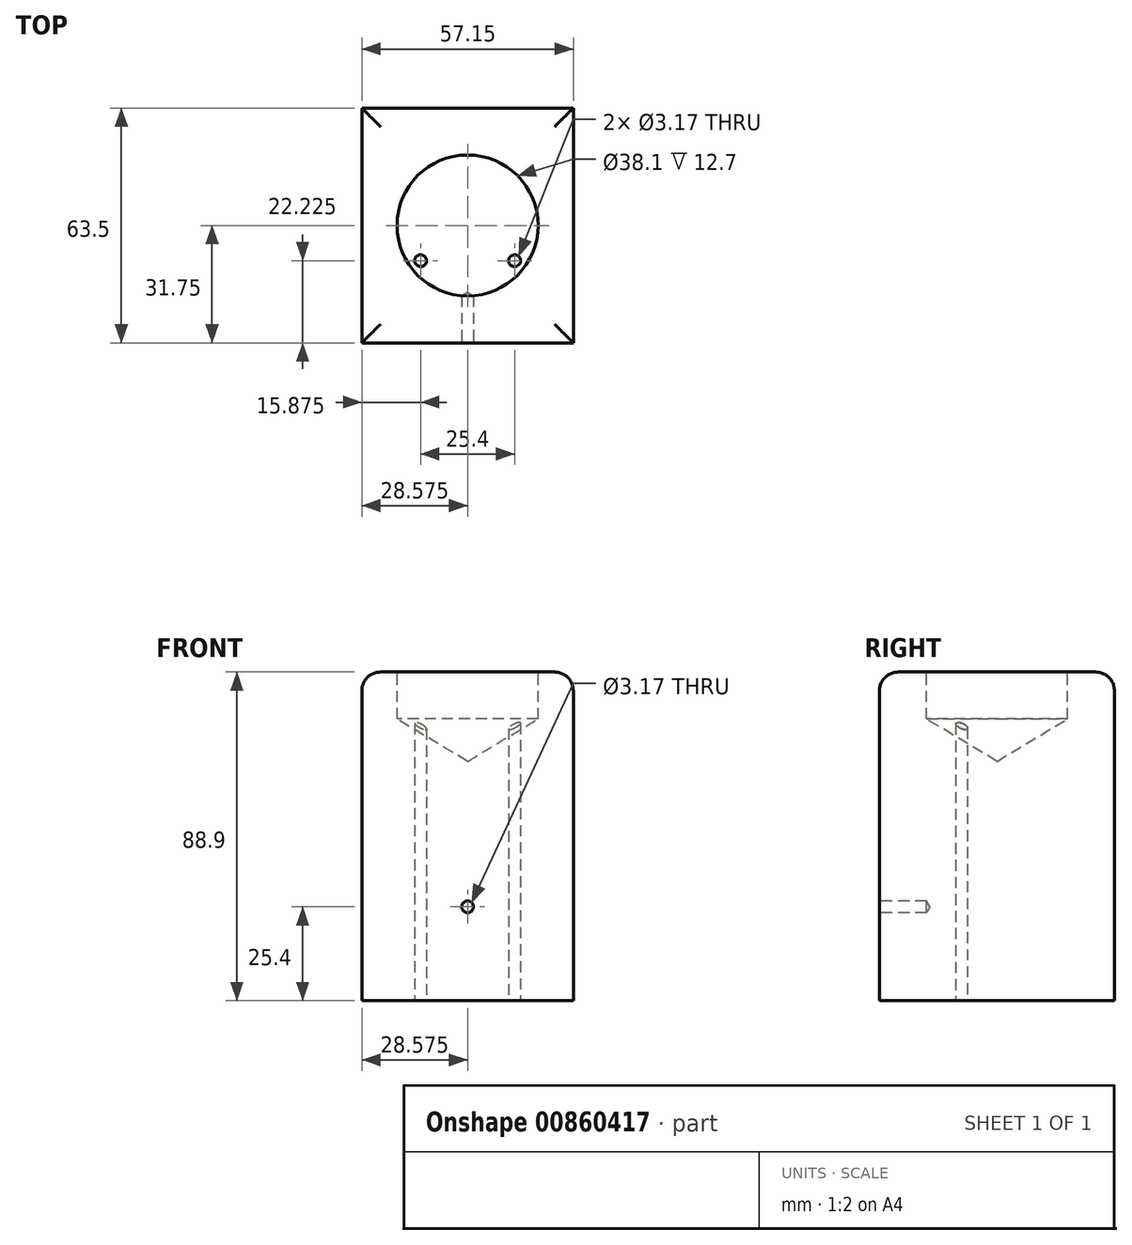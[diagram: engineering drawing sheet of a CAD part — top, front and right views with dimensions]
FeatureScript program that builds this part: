
annotation { "Feature Type Name" : "Feature", "Feature Type Description" : "" }
export const myFeature = defineFeature(function(context is Context, id is Id, definition is map)
    precondition{}
    {
        {
            var Q0;
            Q0=qCreatedBy(makeId("Top.planeOp"),FACE);
            var sketch = newSketch(context, id + "F0", { "sketchPlane" : qUnion([Q0])});
            skLineSegment(sketch, "E0.bottom", {"start": v(0, 0) * mm, "end": v(57.15, 0) * mm});
            skLineSegment(sketch, "E0.top", {"start": v(0, -63.5) * mm, "end": v(57.15, -63.5) * mm});
            skLineSegment(sketch, "E0.left", {"start": v(0, 0) * mm, "end": v(0, -63.5) * mm});
            skLineSegment(sketch, "E0.right", {"start": v(57.15, 0) * mm, "end": v(57.15, -63.5) * mm});
            skSolve(sketch);
        }
        {
            var Q0;
            Q0=makeQuery(id+"F0.imprint","IMPRINT",FACE,{"disambiguationData":[TD([[makeQuery(id+"F0.imprint","IMPRINT",EDGE,{"derivedFrom":sQuery(id+"F0.wireOp",EDGE,"E0.bottom")}),-1.0]])]});
            extrude(context, id + "F1", {"entities" : qUnion([Q0]), "depth" : 88.9 * mm, "offsetDistance" : 25.4 * mm});
        }
        {
            var Q0;
            Q0=makeQuery(id+"F1.opExtrude","CAP_FACE",FACE,{"disambiguationData":[OSD([sQuery(id+"F0.wireOp",EDGE,"E0.bottom"),sQuery(id+"F0.wireOp",EDGE,"E0.top"),sQuery(id+"F0.wireOp",EDGE,"E0.left"),sQuery(id+"F0.wireOp",EDGE,"E0.right")])],"isStart":false});
            var sketch = newSketch(context, id + "F2", { "sketchPlane" : qUnion([Q0])});
            skLineSegment(sketch, "E1", {"start": v(28.58, 0) * mm, "end": v(28.58, -63.5) * mm, "construction": true});
            skLineSegment(sketch, "E2", {"start": v(0, -31.75) * mm, "end": v(57.15, -31.75) * mm, "construction": true});
            skPoint(sketch, "E3", {"position": v(28.58, -31.75) * mm});
            skSolve(sketch);
        }
        {
            var Q0;
            Q0=sQuery(id+"F2.wireOp",VERTEX,"E3");
            var Q1;
            Q1=makeQuery(id+"F1.opExtrude","SWEPT_BODY",BODY,{"disambiguationData":[OSD([sQuery(id+"F0.wireOp",EDGE,"E0.bottom"),sQuery(id+"F0.wireOp",EDGE,"E0.top"),sQuery(id+"F0.wireOp",EDGE,"E0.left"),sQuery(id+"F0.wireOp",EDGE,"E0.right")])]});
            hole(context, id + "F3", {"style" : HoleStyle.SIMPLE, "endStyle" : HoleEndStyle.BLIND, "holeDiameter" : 38.1 * mm, "majorDiameter" : 6.35 * mm, "holeDepth" : 12.7 * mm, "isTappedThrough" : true, "tappedDepth" : 12.7 * mm, "tapClearance" : 3, "locations" : qUnion([Q0]), "scope" : qUnion([Q1])});
        }
        {
            var Q0;
            Q0=makeQuery(id+"F1.opExtrude","CAP_EDGE",EDGE,{"disambiguationData":[OSD([sQuery(id+"F0.wireOp",EDGE,"E0.right")])],"isStart":false});
            var Q1;
            Q1=makeQuery(id+"F1.opExtrude","CAP_EDGE",EDGE,{"disambiguationData":[OSD([sQuery(id+"F0.wireOp",EDGE,"E0.bottom")])],"isStart":false});
            var Q2;
            Q2=makeQuery(id+"F1.opExtrude","CAP_EDGE",EDGE,{"disambiguationData":[OSD([sQuery(id+"F0.wireOp",EDGE,"E0.left")])],"isStart":false});
            var Q3;
            Q3=makeQuery(id+"F1.opExtrude","CAP_EDGE",EDGE,{"disambiguationData":[OSD([sQuery(id+"F0.wireOp",EDGE,"E0.top")])],"isStart":false});
            fillet(context, id + "F4", {"entities" : qUnion([Q0, Q1, Q2, Q3]), "radius" : 5.08 * mm, "tangentPropagation" : true, "allowEdgeOverflow" : false});
        }
        {
            var Q0;
            Q0=makeQuery(id+"F1.opExtrude","SWEPT_FACE",FACE,{"disambiguationData":[OSD([sQuery(id+"F0.wireOp",EDGE,"E0.top")])]});
            var sketch = newSketch(context, id + "F5", { "sketchPlane" : qUnion([Q0])});
            skPoint(sketch, "E4", {"position": v(28.57, 25.4) * mm});
            skSolve(sketch);
        }
        {
            var Q0;
            Q0=sQuery(id+"F5.wireOp",VERTEX,"E4");
            var Q1;
            Q1=makeQuery(id+"F1.opExtrude","SWEPT_BODY",BODY,{"disambiguationData":[OSD([sQuery(id+"F0.wireOp",EDGE,"E0.bottom"),sQuery(id+"F0.wireOp",EDGE,"E0.top"),sQuery(id+"F0.wireOp",EDGE,"E0.left"),sQuery(id+"F0.wireOp",EDGE,"E0.right")])]});
            hole(context, id + "F6", {"style" : HoleStyle.SIMPLE, "endStyle" : HoleEndStyle.BLIND, "holeDiameter" : 3.17 * mm, "majorDiameter" : 6.35 * mm, "holeDepth" : 12.7 * mm, "isTappedThrough" : true, "tappedDepth" : 12.7 * mm, "tapClearance" : 3, "locations" : qUnion([Q0]), "scope" : qUnion([Q1])});
        }
        {
            var Q0;
            Q0=makeQuery(id+"F1.opExtrude","CAP_FACE",FACE,{"disambiguationData":[OSD([sQuery(id+"F0.wireOp",EDGE,"E0.bottom"),sQuery(id+"F0.wireOp",EDGE,"E0.top"),sQuery(id+"F0.wireOp",EDGE,"E0.left"),sQuery(id+"F0.wireOp",EDGE,"E0.right")])],"isStart":true});
            var sketch = newSketch(context, id + "F7", { "sketchPlane" : qUnion([Q0])});
            skPoint(sketch, "E5", {"position": v(41.27, 41.27) * mm});
            skPoint(sketch, "E6", {"position": v(15.87, 41.27) * mm});
            skSolve(sketch);
        }
        {
            var Q0;
            Q0=sQuery(id+"F7.wireOp",VERTEX,"E5");
            var Q1;
            Q1=sQuery(id+"F7.wireOp",VERTEX,"E6");
            var Q2;
            Q2=makeQuery(id+"F1.opExtrude","SWEPT_BODY",BODY,{"disambiguationData":[OSD([sQuery(id+"F0.wireOp",EDGE,"E0.bottom"),sQuery(id+"F0.wireOp",EDGE,"E0.top"),sQuery(id+"F0.wireOp",EDGE,"E0.left"),sQuery(id+"F0.wireOp",EDGE,"E0.right")])]});
            hole(context, id + "F8", {"style" : HoleStyle.SIMPLE, "endStyle" : HoleEndStyle.THROUGH, "holeDiameter" : 3.17 * mm, "majorDiameter" : 6.35 * mm, "isTappedThrough" : true, "tappedDepth" : 12.7 * mm, "tapClearance" : 3, "locations" : qUnion([Q0, Q1]), "scope" : qUnion([Q2])});
        }
    });
